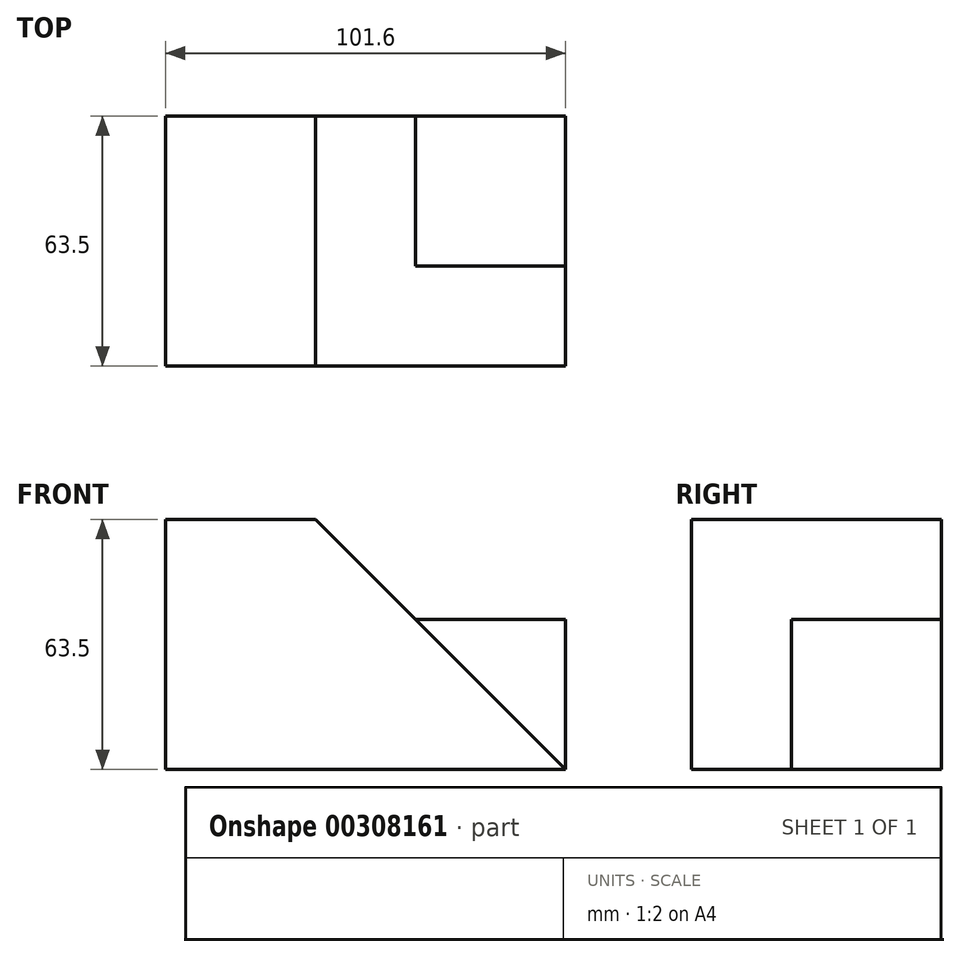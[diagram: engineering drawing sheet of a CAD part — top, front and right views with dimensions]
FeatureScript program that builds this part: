
annotation { "Feature Type Name" : "Feature", "Feature Type Description" : "" }
export const myFeature = defineFeature(function(context is Context, id is Id, definition is map)
    precondition{}
    {
        {
            var Q0;
            Q0=qCreatedBy(makeId("Front.planeOp"),FACE);
            var sketch = newSketch(context, id + "F0", { "sketchPlane" : qUnion([Q0])});
            skLineSegment(sketch, "E0", {"start": v(-22.19, 26.56) * mm, "end": v(15.91, 26.56) * mm});
            skLineSegment(sketch, "E1", {"start": v(-22.19, 26.56) * mm, "end": v(-22.19, -36.94) * mm});
            skLineSegment(sketch, "E2", {"start": v(-22.19, -36.94) * mm, "end": v(79.41, -36.94) * mm});
            skLineSegment(sketch, "E3", {"start": v(15.91, 26.56) * mm, "end": v(79.41, -36.94) * mm});
            skSolve(sketch);
        }
        {
            var Q0;
            Q0=makeQuery(id+"F0.imprint","IMPRINT",FACE,{"disambiguationData":[TD([[makeQuery(id+"F0.imprint","IMPRINT",EDGE,{"derivedFrom":sQuery(id+"F0.wireOp",EDGE,"E0")}),-1.0]])]});
            extrude(context, id + "F1", {"entities" : qUnion([Q0]), "oppositeDirection" : true, "depth" : 63.5 * mm});
        }
        {
            var Q0;
            Q0=makeQuery(id+"F1.opExtrude","CAP_FACE",FACE,{"disambiguationData":[OSD([sQuery(id+"F0.wireOp",EDGE,"E0"),sQuery(id+"F0.wireOp",EDGE,"E1"),sQuery(id+"F0.wireOp",EDGE,"E2"),sQuery(id+"F0.wireOp",EDGE,"E3")])],"isStart":false});
            var sketch = newSketch(context, id + "F2", { "sketchPlane" : qUnion([Q0])});
            skLineSegment(sketch, "E4", {"start": v(-79.41, -36.94) * mm, "end": v(-79.41, 1.16) * mm});
            skLineSegment(sketch, "E5", {"start": v(-79.41, 1.16) * mm, "end": v(-41.31, 1.16) * mm});
            skSolve(sketch);
        }
        {
            var Q0;
            {var subQ0=sQuery(id+"F2.wireOp",EDGE,"E4");Q0=makeQuery(id+"F2.imprint","IMPRINT",FACE,{"disambiguationData":[TD([[makeQuery(id+"F2.imprint","IMPRINT",EDGE,{"derivedFrom":subQ0}),-1.0]])]});}
            extrude(context, id + "F3", {"entities" : qUnion([Q0]), "operationType" : NewBodyOperationType.ADD, "oppositeDirection" : true, "depth" : 38.1 * mm});
        }
    });
